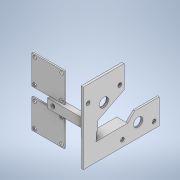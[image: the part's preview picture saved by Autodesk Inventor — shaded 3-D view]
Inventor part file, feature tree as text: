
AUTODESK INVENTOR PART (.ipt)
format: ipt  version: 2020.2 (Build 242310000, 310)  size: 289,792 bytes
history: native  units: mm
features: sketch x11, extrude x8, hole x4, projected_geometry x2
ambient origin geometry x8: Origin, YZ Plane, XZ Plane, XY Plane, X Axis, Y Axis, Z Axis, Center Point
bodies: Body1 (feature_tree)
feature tree (25):
  extrude  "Extrusion7"  Depth=6.08mm
  hole  "Hole4"  [1 undecoded]
  sketch  "Sketch16"  dims[d70=12.16mm d71=10.0mm]
  extrude  "Extrusion8"  Depth=10.0mm
  hole  "Hole5"  [1 undecoded]
  extrude  "Extrusion9"  Depth=32.05mm
  extrude  "Extrusion10"  Depth=32.05mm
  extrude  "Extrusion11"  Depth=3.0mm
  hole  "Hole6"  [1 undecoded]
  hole  "Hole7"  [1 undecoded]
  extrude  "Extrusion13"  Depth=10.0mm
  extrude  "Extrusion14"  Depth=1.5mm TaperAngle=0.0deg
  extrude  "Extrusion15"  Depth=4.0mm TaperAngle=0.0deg
  sketch  "Sketch14"  dims[d66=6.08mm d67=6.08mm]
  sketch  "Sketch15"  dims[d68=5.0mm d69=90.0deg]
  sketch  "Sketch17"  dims[d72=2.0mm d73=0.0mm]
  projected_geometry  "Projected Loop2"
  sketch  "Sketch18"  dims[d74=4.5mm d75=6.0mm d76=9.4mm d77=2.0mm d78=90.0deg d79=8.0mm d80=20.594885mm d81=10.0mm]
  projected_geometry  "Projected Loop3"
  sketch  "Sketch19"  dims[d82=35.7mm d83=32.05mm]
  sketch  "Sketch21"  dims[d84=35.7mm d85=32.05mm]
  sketch  "Sketch22"  dims[d86=3.0mm d87=3.0mm]
  sketch  "Sketch23"  dims[d88=29.7mm d89=26.05mm]
  sketch  "Sketch24"  dims[d90=3.0mm d91=3.0mm]
  sketch  "Sketch25"  dims[d92=29.7mm d93=26.05mm d94=1.5mm d95=0.0mm d96=3.9mm d97=6.0mm d98=8.2mm d99=2.0mm d100=90.0deg d101=8.0mm d102=20.594885mm d103=4.0mm d104=0.0mm d105=35.0mm d106=0.0mm d107=10.0mm d108=50.0mm d109=90.0deg d110=45.0mm d111=90.0deg d112=25.0mm d113=2.5mm d114=0.0mm d118=14.05mm d119=90.0deg d120=6.713mm d121=90.0deg d122=10.0mm d123=6.0mm d124=8.2mm d125=2.0mm d126=90.0deg d127=8.0mm d128=20.594885mm d129=8.0mm d130=90.0deg d131=17.5mm d132=90.0deg d133=35.0mm d134=4.2mm d135=6.0mm d136=8.2mm d137=2.0mm d138=90.0deg d139=8.0mm d140=20.594885mm d141=9.0mm d142=90.0deg d145=35.0mm d146=0.0mm d147=11.0mm d148=135.0deg d149=20.0mm d150=35.0mm d151=0.0mm d152=20.0mm d153=90.0deg d154=90.0deg d155=11.45mm d156=4.669mm d157=90.0deg d158=8.0mm d159=17.5mm d160=35.0mm d161=4.2mm d162=4.2mm d163=10.0mm d164=2.0mm d165=0.0mm d166=2.0mm d167=0.0mm d168=35.0mm d169=2.0mm d170=10.0mm d171=0.0mm d172=10.0mm]
note: 4 required parameter values undecoded (feature->parameter linkage not recoverable at this tier; creation-order binding heuristic only, values carry confidence <= 0.55)
